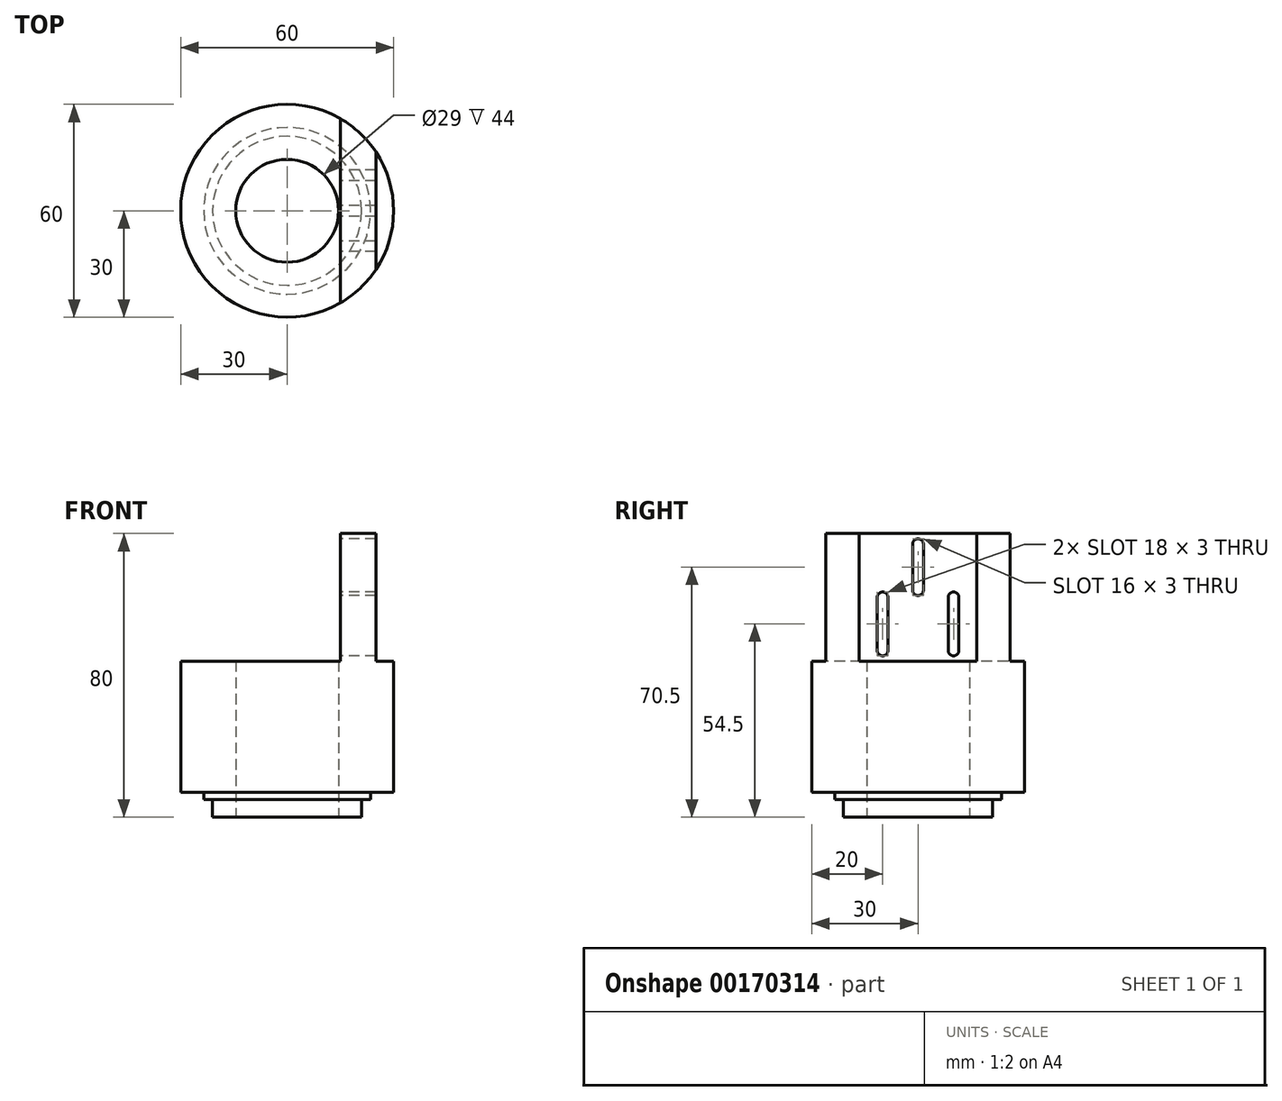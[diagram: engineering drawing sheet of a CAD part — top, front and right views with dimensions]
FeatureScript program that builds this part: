
annotation { "Feature Type Name" : "Feature", "Feature Type Description" : "" }
export const myFeature = defineFeature(function(context is Context, id is Id, definition is map)
    precondition{}
    {
        {
            var Q0;
            Q0=qCreatedBy(makeId("Top.planeOp"),FACE);
            var sketch = newSketch(context, id + "F0", { "sketchPlane" : qUnion([Q0])});
            skCircle(sketch, "E0", {"center": v(0, 0) * mm, "radius": 30 * mm});
            skCircle(sketch, "E1", {"center": v(0, 0) * mm, "radius": 14.5 * mm});
            skSolve(sketch);
        }
        {
            var Q0;
            Q0 = qSketchRegion(id + "F0", true);
            extrude(context, id + "F1", {"entities" : qUnion([Q0]), "depth" : 73 * mm});
        }
        {
            var Q0;
            Q0=makeQuery(id+"F1.opExtrude","CAP_FACE",FACE,{"disambiguationData":[OSD([sQuery(id+"F0.wireOp",EDGE,"E0"),sQuery(id+"F0.wireOp",EDGE,"E1")])],"isStart":true});
            var sketch = newSketch(context, id + "F2", { "sketchPlane" : qUnion([Q0])});
            skCircle(sketch, "E2", {"center": v(0, 0) * mm, "radius": 23.5 * mm});
            skCircle(sketch, "E3", {"center": v(0, 0) * mm, "radius": 14.5 * mm});
            skSolve(sketch);
        }
        {
            var Q0;
            Q0 = qSketchRegion(id + "F2", true);
            extrude(context, id + "F3", {"entities" : qUnion([Q0]), "operationType" : NewBodyOperationType.ADD, "depth" : 2 * mm});
        }
        {
            var Q0;
            Q0=makeQuery(id+"F3.opExtrude","CAP_FACE",FACE,{"disambiguationData":[OSD([sQuery(id+"F2.wireOp",EDGE,"E2"),sQuery(id+"F2.wireOp",EDGE,"E3")])],"isStart":false});
            var sketch = newSketch(context, id + "F4", { "sketchPlane" : qUnion([Q0])});
            skCircle(sketch, "E4", {"center": v(0, 0) * mm, "radius": 21 * mm});
            skCircle(sketch, "E5", {"center": v(0, 0) * mm, "radius": 14.5 * mm});
            skSolve(sketch);
        }
        {
            var Q0;
            Q0 = qSketchRegion(id + "F4", true);
            extrude(context, id + "F5", {"entities" : qUnion([Q0]), "operationType" : NewBodyOperationType.ADD, "depth" : 5 * mm});
        }
        {
            var Q0;
            Q0=makeQuery(id+"F1.opExtrude","CAP_FACE",FACE,{"disambiguationData":[OSD([sQuery(id+"F0.wireOp",EDGE,"E0"),sQuery(id+"F0.wireOp",EDGE,"E1")])],"isStart":false});
            var sketch = newSketch(context, id + "F6", { "sketchPlane" : qUnion([Q0])});
            skLineSegment(sketch, "E6", {"start": v(15, 25.98) * mm, "end": v(15, -25.98) * mm});
            skArc(sketch, "E7", {"start": v(15, 25.98) * mm, "mid": v(-30, 0) * mm, "end": v(15, -25.98) * mm});
            skLineSegment(sketch, "E8", {"start": v(25, 16.58) * mm, "end": v(25, -16.58) * mm});
            skArc(sketch, "E9.trimOffspring", {"start": v(25, -16.58) * mm, "mid": v(30, 0) * mm, "end": v(25, 16.58) * mm});
            skSolve(sketch);
        }
        {
            var Q0;
            Q0=makeQuery(id+"F6.imprint","IMPRINT",FACE,{"disambiguationData":[TD([[makeQuery(id+"F6.imprint","IMPRINT",EDGE,{"derivedFrom":sQuery(id+"F6.wireOp",EDGE,"E6")}),-1.0]])]});
            var Q1;
            Q1=makeQuery(id+"F6.imprint","IMPRINT",FACE,{"disambiguationData":[TD([[makeQuery(id+"F6.imprint","IMPRINT",EDGE,{"derivedFrom":sQuery(id+"F6.wireOp",EDGE,"E8")}),1.0]])]});
            extrude(context, id + "F7", {"entities" : qUnion([Q0, Q1]), "operationType" : NewBodyOperationType.REMOVE, "oppositeDirection" : true, "depth" : 36 * mm});
        }
        {
            var Q0;
            Q0=makeQuery(id+"F7.boolean.opBoolean","COPY",FACE,{"derivedFrom":makeQuery(id+"F7.opExtrude","SWEPT_FACE",FACE,{"disambiguationData":[OSD([sQuery(id+"F6.wireOp",EDGE,"E6")])]})});
            var sketch = newSketch(context, id + "F8", { "sketchPlane" : qUnion([Q0])});
            skArc(sketch, "E10", {"start": v(-11.5, 40) * mm, "mid": v(-10, 38.5) * mm, "end": v(-8.5, 40) * mm});
            skArc(sketch, "E11", {"start": v(8.5, 40) * mm, "mid": v(10, 38.5) * mm, "end": v(11.5, 40) * mm});
            skArc(sketch, "E12", {"start": v(-1.5, 57) * mm, "mid": v(0, 55.5) * mm, "end": v(1.5, 57) * mm});
            skArc(sketch, "E13", {"start": v(-8.5, 55) * mm, "mid": v(-10, 56.5) * mm, "end": v(-11.5, 55) * mm});
            skArc(sketch, "E14", {"start": v(1.5, 70) * mm, "mid": v(0, 71.5) * mm, "end": v(-1.5, 70) * mm});
            skArc(sketch, "E15", {"start": v(11.5, 55) * mm, "mid": v(10, 56.5) * mm, "end": v(8.5, 55) * mm});
            skLineSegment(sketch, "E16", {"start": v(-11.5, 55) * mm, "end": v(-11.5, 40) * mm});
            skLineSegment(sketch, "E17", {"start": v(-8.5, 55) * mm, "end": v(-8.5, 40) * mm});
            skLineSegment(sketch, "E18", {"start": v(-1.5, 70) * mm, "end": v(-1.5, 57) * mm});
            skLineSegment(sketch, "E19", {"start": v(1.5, 70) * mm, "end": v(1.5, 57) * mm});
            skLineSegment(sketch, "E20", {"start": v(8.5, 55) * mm, "end": v(8.5, 40) * mm});
            skLineSegment(sketch, "E21", {"start": v(11.5, 55) * mm, "end": v(11.5, 40) * mm});
            skSolve(sketch);
        }
        {
            var Q0;
            Q0 = qSketchRegion(id + "F8", true);
            extrude(context, id + "F9", {"entities" : qUnion([Q0]), "operationType" : NewBodyOperationType.REMOVE, "endBound" : BoundingType.THROUGH_ALL, "oppositeDirection" : true, "depth" : 25 * mm});
        }
    });
